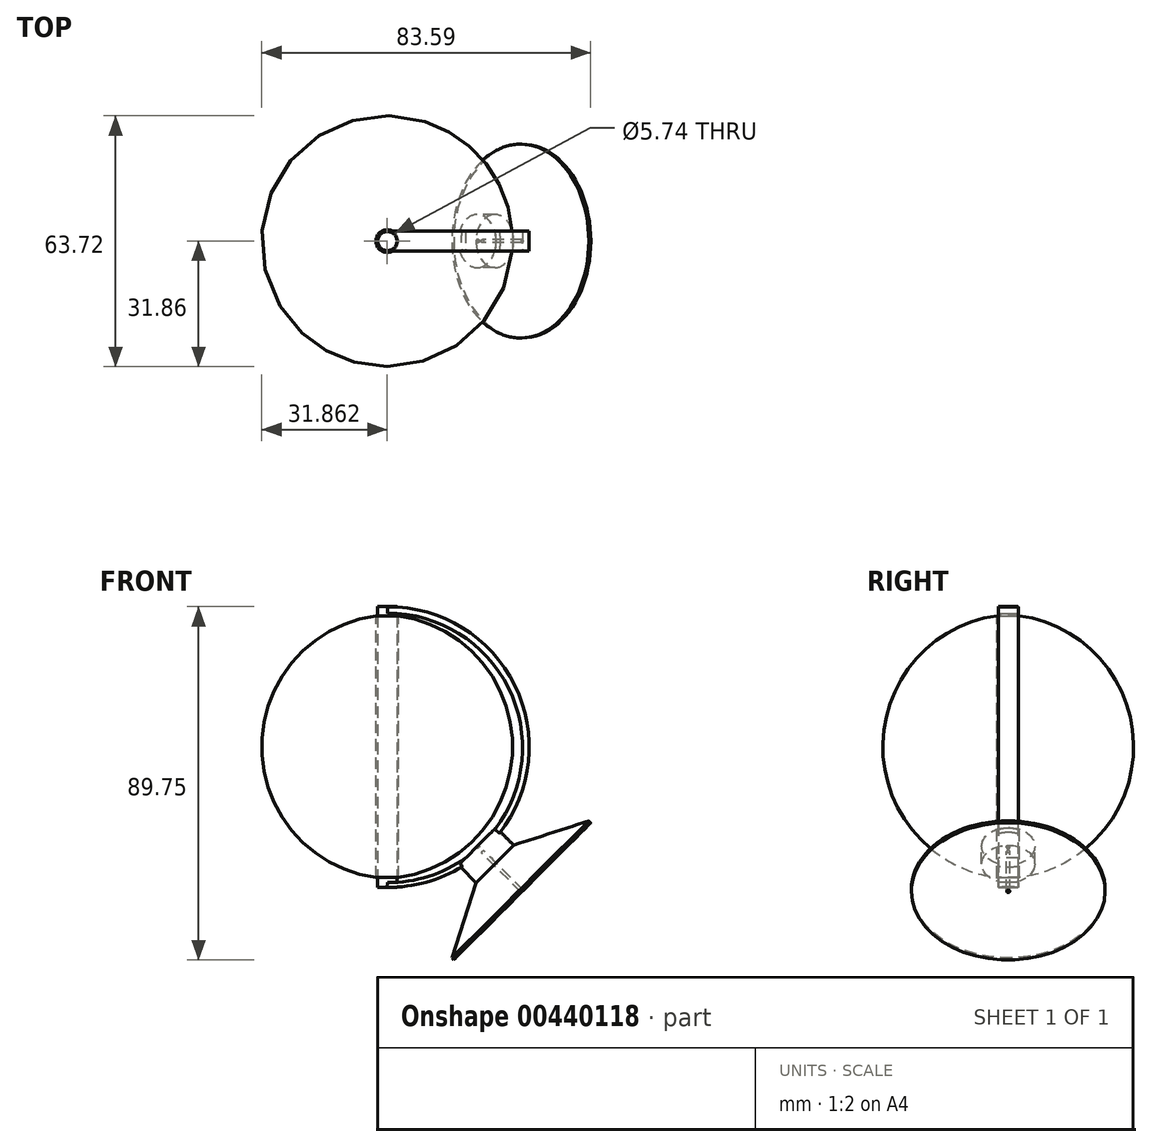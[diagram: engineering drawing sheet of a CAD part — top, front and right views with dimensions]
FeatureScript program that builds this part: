
annotation { "Feature Type Name" : "Feature", "Feature Type Description" : "" }
export const myFeature = defineFeature(function(context is Context, id is Id, definition is map)
    precondition{}
    {
        {
            var Q0;
            Q0=qCreatedBy(makeId("Front.planeOp"),FACE);
            var sketch = newSketch(context, id + "F0", { "sketchPlane" : qUnion([Q0])});
            skLineSegment(sketch, "E0", {"start": v(0, 42.37) * mm, "end": v(0, -24.17) * mm});
            skLineSegment(sketch, "E1", {"start": v(-2.87, 42.37) * mm, "end": v(-2.87, -24.53) * mm, "construction": true});
            skArc(sketch, "E2", {"start": v(0, -24.17) * mm, "mid": v(29, 9.1) * mm, "end": v(0, 42.37) * mm});
            skSolve(sketch);
        }
        {
            var Q0;
            Q0=makeQuery(id+"F0.imprint","IMPRINT",FACE,{"disambiguationData":[TD([[makeQuery(id+"F0.imprint","IMPRINT",EDGE,{"derivedFrom":sQuery(id+"F0.wireOp",EDGE,"E0")}),1.0]])]});
            var Q1;
            Q1=sQuery(id+"F0.wireOp",EDGE,"E1");
            revolve(context, id + "F1", {"entities" : qUnion([Q0]), "axis" : qUnion([Q1]), "revolveType" : RevolveType.FULL});
        }
        {
            var Q0;
            Q0=qCreatedBy(makeId("Top.planeOp"),FACE);
            var sketch = newSketch(context, id + "F2", { "sketchPlane" : qUnion([Q0])});
            skCircle(sketch, "E3", {"center": v(-2.81, 0) * mm, "radius": 2.44 * mm});
            skSolve(sketch);
        }
        {
            var Q0;
            Q0=makeQuery(id+"F2.imprint","IMPRINT",FACE,{"disambiguationData":[TD([[makeQuery(id+"F2.imprint","IMPRINT",EDGE,{"derivedFrom":sQuery(id+"F2.wireOp",EDGE,"E3")}),1.0]])]});
            extrude(context, id + "F3", {"entities" : qUnion([Q0]), "depth" : 44.7 * mm, "hasSecondDirection" : true, "secondDirectionOppositeDirection" : true, "secondDirectionDepth" : 26.67 * mm});
        }
        {
            var Q0;
            Q0=qCreatedBy(makeId("Front.planeOp"),FACE);
            var sketch = newSketch(context, id + "F4", { "sketchPlane" : qUnion([Q0])});
            skArc(sketch, "E4", {"start": v(-2.92, -26.6) * mm, "mid": v(33.2, 8.91) * mm, "end": v(-2.75, 44.6) * mm});
            skArc(sketch, "E5", {"start": v(-2.75, -25.44) * mm, "mid": v(31.53, 8.78) * mm, "end": v(-2.75, 43) * mm});
            skLineSegment(sketch, "E6", {"start": v(-2.75, 44.6) * mm, "end": v(-2.75, 43) * mm});
            skLineSegment(sketch, "E7", {"start": v(-2.75, -25.44) * mm, "end": v(-2.92, -26.6) * mm});
            skSolve(sketch);
        }
        {
            var Q0;
            Q0=makeQuery(id+"F4.imprint","IMPRINT",FACE,{"disambiguationData":[TD([[makeQuery(id+"F4.imprint","IMPRINT",EDGE,{"derivedFrom":sQuery(id+"F4.wireOp",EDGE,"E4")}),1.0]])]});
            extrude(context, id + "F5", {"entities" : qUnion([Q0]), "operationType" : NewBodyOperationType.ADD, "oppositeDirection" : true, "depth" : 2.54 * mm, "hasSecondDirection" : true, "secondDirectionOppositeDirection" : false, "secondDirectionDepth" : 2.54 * mm});
        }
        {
            var Q0;
            Q0=qCreatedBy(makeId("Front.planeOp"),FACE);
            var sketch = newSketch(context, id + "F6", { "sketchPlane" : qUnion([Q0])});
            skLineSegment(sketch, "E8", {"start": v(24.8, -11.43) * mm, "end": v(20.3, -15.92) * mm});
            skLineSegment(sketch, "E9", {"start": v(20.3, -15.92) * mm, "end": v(24.8, -20.41) * mm});
            skLineSegment(sketch, "E10", {"start": v(24.8, -20.41) * mm, "end": v(29.29, -15.92) * mm});
            skLineSegment(sketch, "E11", {"start": v(29.29, -15.92) * mm, "end": v(24.8, -11.43) * mm});
            skLineSegment(sketch, "E12", {"start": v(24.8, -20.41) * mm, "end": v(31.74, -27.36) * mm});
            skLineSegment(sketch, "E13", {"start": v(31.74, -27.36) * mm, "end": v(48.86, -10.24) * mm});
            skLineSegment(sketch, "E14", {"start": v(48.86, -10.24) * mm, "end": v(48.37, -9.75) * mm});
            skLineSegment(sketch, "E15", {"start": v(48.37, -9.75) * mm, "end": v(29.29, -15.92) * mm});
            skLineSegment(sketch, "E16", {"start": v(19.9, -16.08) * mm, "end": v(31.17, -27.36) * mm, "construction": true});
            skSolve(sketch);
        }
        {
            var Q0;
            Q0=makeQuery(id+"F6.imprint","IMPRINT",FACE,{"disambiguationData":[TD([[makeQuery(id+"F6.imprint","IMPRINT",EDGE,{"derivedFrom":sQuery(id+"F6.wireOp",EDGE,"E8")}),1.0]])]});
            var Q1;
            Q1=makeQuery(id+"F6.imprint","IMPRINT",FACE,{"disambiguationData":[TD([[makeQuery(id+"F6.imprint","IMPRINT",EDGE,{"derivedFrom":sQuery(id+"F6.wireOp",EDGE,"E10")}),-1.0]])]});
            var Q2;
            Q2=sQuery(id+"F6.wireOp",EDGE,"E16");
            revolve(context, id + "F7", {"operationType" : NewBodyOperationType.ADD, "entities" : qUnion([Q0, Q1]), "axis" : qUnion([Q2]), "revolveType" : RevolveType.FULL});
        }
    });
